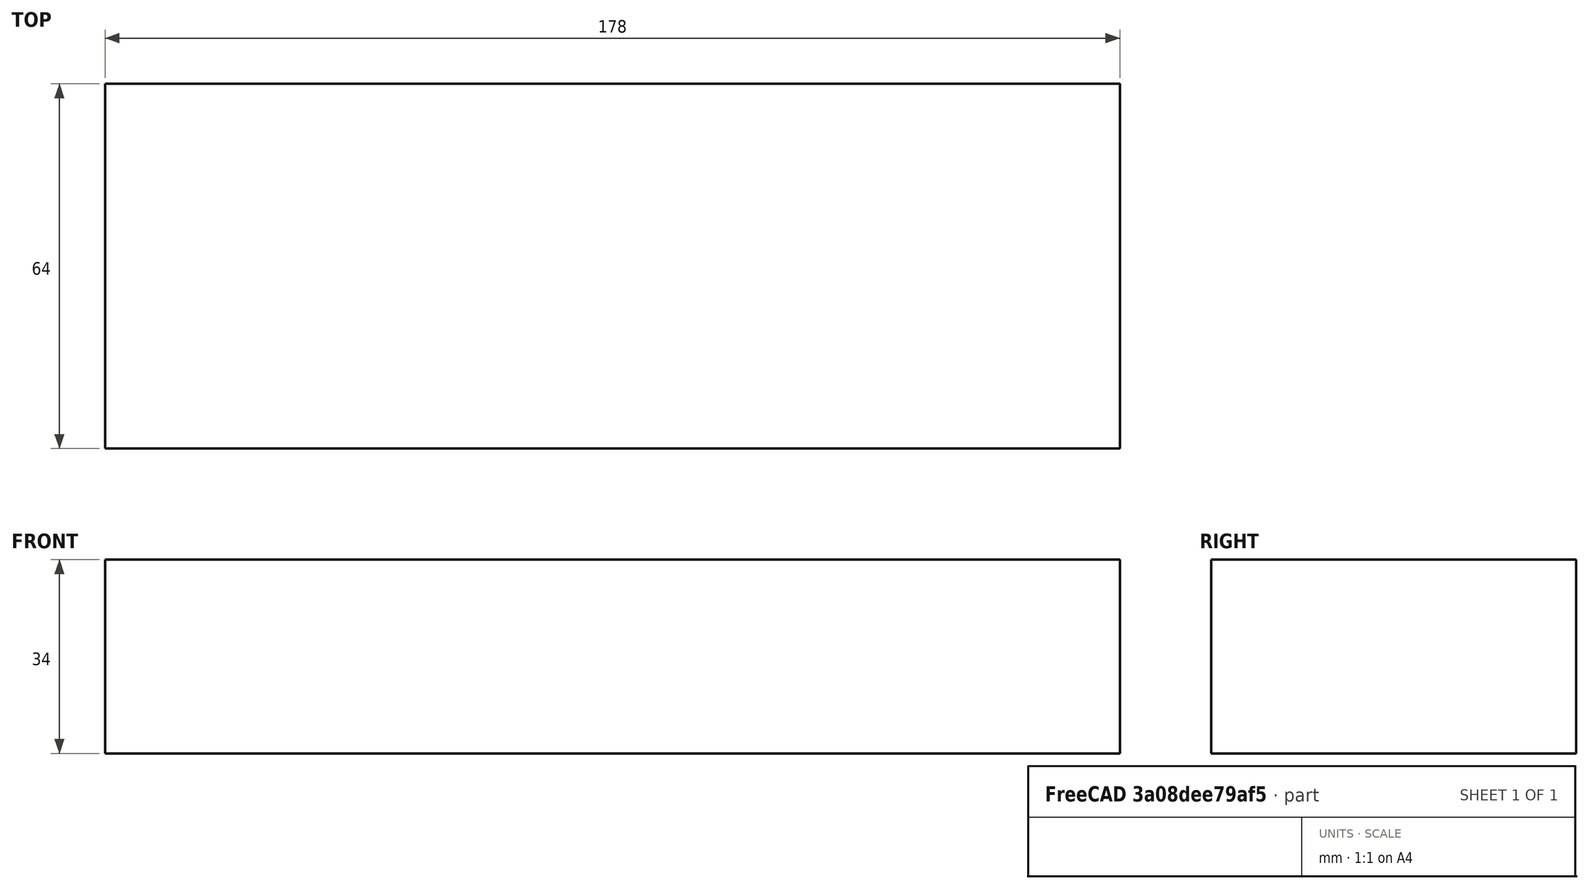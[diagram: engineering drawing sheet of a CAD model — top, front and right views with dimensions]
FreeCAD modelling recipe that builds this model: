
FCSTD DOCUMENT  (FreeCAD 0.16R6706 (Git))
Label: Batterie 12V
License: All rights reserved
LicenseURL: http://en.wikipedia.org/wiki/All_rights_reserved
objects: Sketcher::SketchObject×1, PartDesign::Pad×1
note: 3 computed .brp shape members not serialized (recipe doc carries the construction recipe); baked Part::Feature solids carry a one-line shape summary decoded from their .brp

FEATURE [Sketcher::SketchObject] Sketch
  sketch-geometry (4):
    g0: LineSegment StartX=0 StartY=0 StartZ=0 EndX=-178 EndY=0 EndZ=0
    g1: LineSegment StartX=-178 StartY=0 StartZ=0 EndX=-178 EndY=64 EndZ=0
    g2: LineSegment StartX=-178 StartY=64 StartZ=0 EndX=0 EndY=64 EndZ=0
    g3: LineSegment StartX=0 StartY=64 StartZ=0 EndX=0 EndY=0 EndZ=0
  constraints (11):
    c: Coincident(g0,g1)
    c: Coincident(g1,g2)
    c: Coincident(g2,g3)
    c: Coincident(g3,g0)
    c: Horizontal(g0)
    c: Horizontal(g2)
    c: Vertical(g1)
    c: Vertical(g3)
    c: DistanceX(g2,g2) = 178
    c: DistanceY(g3,g3) = 64
    c: Coincident(g0,g-1)
FEATURE [PartDesign::Pad] Pad
  Length = 34
  Length2 = 100
  Sketch = -> Sketch
  Type = 0
